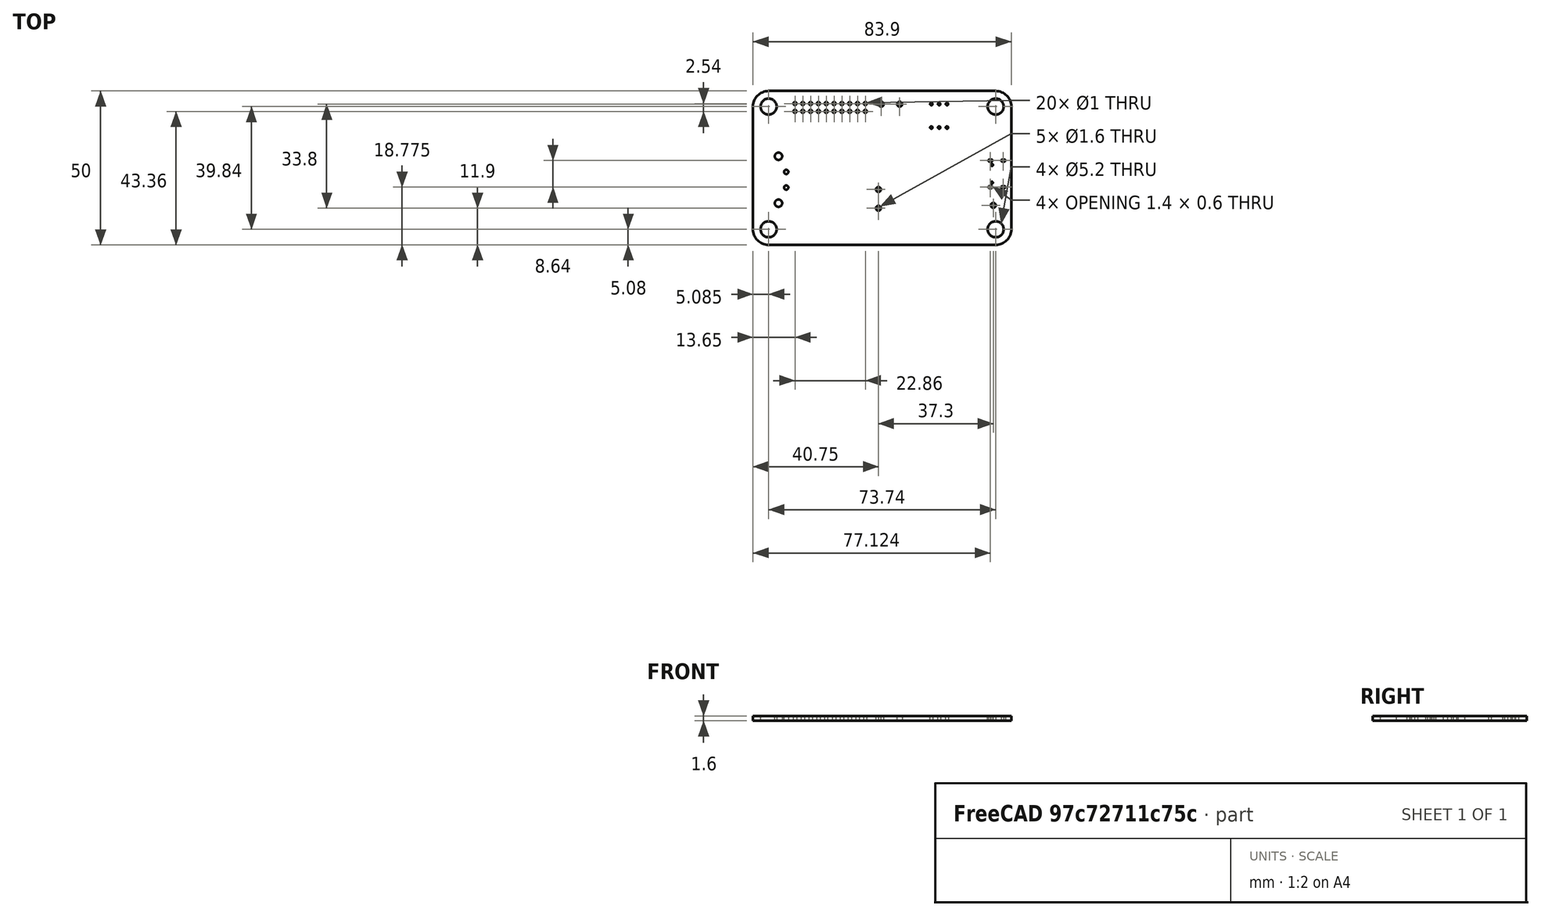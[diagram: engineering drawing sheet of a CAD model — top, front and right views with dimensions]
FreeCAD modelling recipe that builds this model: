
FCSTD DOCUMENT  (FreeCAD 0.21R33771 (Git))
Label: Main-Module
License: All rights reserved
LicenseURL: http://en.wikipedia.org/wiki/All_rights_reserved
objects: App::Part×3, PartDesign::CoordinateSystem×1, Part::Feature×1, Sketcher::SketchObject×1
note: 3 computed .brp shape members not serialized (recipe doc carries the construction recipe); baked Part::Feature solids carry a one-line shape summary decoded from their .brp

FEATURE [PartDesign::CoordinateSystem] Local_CS_6c42
  AttacherType = Attacher::AttachEngine3D
  MapMode = 2
  Support = -> [X_Axis001]
FEATURE [Part::Feature] Pcb_6c42
  shape: bbox 83.9 x 50 x 1.6 mm, 75 faces (baked)
FEATURE [Sketcher::SketchObject] PCB_Sketch_6c42
  FullyConstrained = true
  sketch-geometry (12):
    g0: LineSegment StartX=115.734 StartY=-85.6489 StartZ=0 EndX=181.774 EndY=-85.6489 EndZ=0
    g1: LineSegment StartX=186.854 StartY=-90.7289 StartZ=0 EndX=186.854 EndY=-128.829 EndZ=0
    g2: LineSegment StartX=110.654 StartY=-128.829 StartZ=0 EndX=110.654 EndY=-90.7289 EndZ=0
    g3: LineSegment StartX=181.774 StartY=-133.909 StartZ=0 EndX=115.734 EndY=-133.909 EndZ=0
    g4: ArcOfCircle CenterX=181.774 CenterY=-90.7289 CenterZ=0 NormalX=0 NormalY=0 NormalZ=-1 AngleXU=1.5708 Radius=5.08 StartAngle=6.28319 EndAngle=7.85398
    g5: ArcOfCircle CenterX=115.734 CenterY=-90.7289 CenterZ=0 NormalX=0 NormalY=0 NormalZ=-1 AngleXU=3.01383e-07 Radius=5.08 StartAngle=6.28319 EndAngle=7.85398
    g6: ArcOfCircle CenterX=115.734 CenterY=-128.829 CenterZ=0 NormalX=0 NormalY=0 NormalZ=-1 AngleXU=-1.5708 Radius=5.08 StartAngle=6.28319 EndAngle=7.85398
    g7: ArcOfCircle CenterX=181.774 CenterY=-128.829 CenterZ=0 NormalX=0 NormalY=0 NormalZ=-1 AngleXU=-3.14159 Radius=5.08 StartAngle=6.28319 EndAngle=7.85398
    g8: Circle CenterX=181.774 CenterY=-90.7289 CenterZ=0 NormalX=0 NormalY=0 NormalZ=1 AngleXU=0 Radius=2.54
    g9: Circle CenterX=115.734 CenterY=-128.829 CenterZ=0 NormalX=0 NormalY=0 NormalZ=1 AngleXU=0 Radius=2.54
    g10: Circle CenterX=181.774 CenterY=-128.829 CenterZ=0 NormalX=0 NormalY=0 NormalZ=1 AngleXU=0 Radius=2.54
    g11: Circle CenterX=115.734 CenterY=-90.7289 CenterZ=0 NormalX=0 NormalY=0 NormalZ=1 AngleXU=0 Radius=2.54
  constraints (36):
    c: Coincident(g2,g6)
    c: Coincident(g2,g5)
    c: Coincident(g3,g6)
    c: Coincident(g0,g5)
    c: Coincident(g3,g7)
    c: Coincident(g0,g4)
    c: Coincident(g1,g7)
    c: Coincident(g1,g4)
    c: Vertical(g2)
    c: Vertical(g1)
    c: Horizontal(g3)
    c: Horizontal(g0)
    c: DistanceX(g2,g1) = 76.2
    c: DistanceY(g7,g4) = 38.1
    c: Coincident(g6,g9)
    c: Coincident(g4,g8)
    c: Coincident(g7,g10)
    c: Horizontal(g7,g6)
    c: Horizontal(g4,g5)
    c: Equal(g1,g2)
    c: Equal(g3,g0)
    c: Coincident(g5,g11)
    c: Vertical(g3,g6)
    c: Vertical(g6,g5)
    c: Vertical(g5,g0)
    c: Horizontal(g5,g2)
    c: Horizontal(g2,g6)
    c: Horizontal(g1,g4)
    c: Vertical(g7,g3)
    c: Radius(g9) = 2.54
    c: Radius(g11) = 2.54
    c: Radius(g8) = 2.54
    c: Radius(g10) = 2.54
    c: DistanceX(g1) = 186.854
    c: DistanceY(g1) = -90.7289
    c: Radius(g4) = 5.08
FEATURE [App::Part] Board_Geoms_6c42
  Group = -> [Pcb_6c42,PCB_Sketch_6c42]
  Origin = -> Origin
FEATURE [App::Part] Step_Models_6c42
  Origin = -> Origin002
FEATURE [App::Part] Board_6c42  label="Main-Module"
  Group = -> [Local_CS_6c42,Board_Geoms_6c42,Step_Models_6c42]
  Origin = -> Origin001
